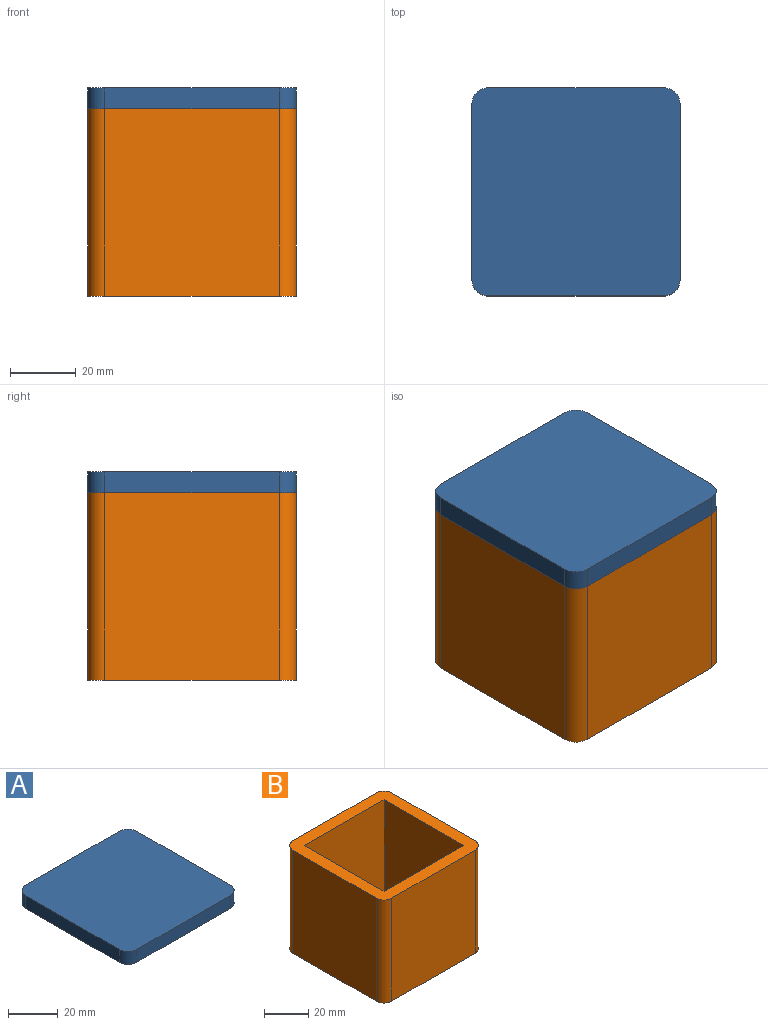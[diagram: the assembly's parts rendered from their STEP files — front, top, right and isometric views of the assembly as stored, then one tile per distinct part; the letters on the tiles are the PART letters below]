
ASSEMBLY  parts=2 mates=1
PART A: 15 faces, bbox 63.5x63.5x12.7 mm
  f0: plane 48.26x6.35mm, normal (1,0,0), area 306.5mm2, adj f1,f3,f4,f10
  f1: plane 48.26x6.35mm, normal (0,1,0), area 306.5mm2, adj f0,f2,f4,f10
  f2: plane 48.26x6.35mm, normal (-1,0,0), area 306.5mm2, adj f1,f3,f4,f10
  f3: plane 48.26x6.35mm, normal (0,-1,0), area 306.5mm2, adj f0,f2,f4,f10
  f4: plane 48.26x48.26mm, normal (0,0,-1), area 2329mm2, adj f0,f1,f2,f3
  f5: plane 53.34x6.35mm, normal (1,0,0), area 338.7mm2, adj f9,f10,f11,f14
  f6: plane 53.34x6.35mm, normal (0,1,0), area 338.7mm2, adj f9,f10,f11,f12
  f7: plane 53.34x6.35mm, normal (-1,0,0), area 338.7mm2, adj f9,f10,f12,f13
  f8: plane 53.34x6.35mm, normal (0,-1,0), area 338.7mm2, adj f9,f10,f13,f14
  f9: plane 63.5x63.5mm, normal (0,0,1), area 4010.1mm2, adj f5,f6,f7,f8,f11,f12,f13,f14
  f10: plane 63.5x63.5mm, normal (0,0,-1), area 1681.1mm2, adj f0,f1,f2,f3,f5,f6,f7,f8
  f11: cylinder r=5.08mm len=6.35mm, axis (0,0,1), area 50.7mm2, adj f5,f6,f9,f10
  f12: cylinder r=5.08mm len=6.35mm, axis (0,0,-1), area 50.7mm2, adj f6,f7,f9,f10
  f13: cylinder r=5.08mm len=6.35mm, axis (0,0,1), area 50.7mm2, adj f7,f8,f9,f10
  f14: cylinder r=5.08mm len=6.35mm, axis (0,0,-1), area 50.7mm2, adj f5,f8,f9,f10
PART B: 15 faces, bbox 63.5x63.5x57.2 mm
  f0: plane 63.5x63.5mm, normal (0,0,1), area 1429.5mm2, adj f1,f2,f3,f4,f5,f6,f7,f8
  f1: plane 57.15x53.34mm, normal (0,-1,0), area 3048.4mm2, adj f0,f10,f11,f13
  f2: plane 57.15x53.34mm, normal (-1,0,0), area 3048.4mm2, adj f0,f10,f11,f12
  f3: plane 57.15x53.34mm, normal (0,1,0), area 3048.4mm2, adj f0,f10,f12,f14
  f4: plane 57.15x53.34mm, normal (1,0,0), area 3048.4mm2, adj f0,f10,f13,f14
  f5: plane 50.8x50.8mm, normal (0,1,0), area 2580.6mm2, adj f0,f6,f8,f9
  f6: plane 50.8x50.8mm, normal (1,0,0), area 2580.6mm2, adj f0,f5,f7,f9
  f7: plane 50.8x50.8mm, normal (0,-1,0), area 2580.6mm2, adj f0,f6,f8,f9
  f8: plane 50.8x50.8mm, normal (-1,0,0), area 2580.6mm2, adj f0,f5,f7,f9
  f9: plane 50.8x50.8mm, normal (0,0,1), area 2580.6mm2, adj f5,f6,f7,f8
  f10: plane 63.5x63.5mm, normal (0,0,-1), area 4010.1mm2, adj f1,f2,f3,f4,f11,f12,f13,f14
  f11: cylinder r=5.08mm len=57.15mm, axis (0,0,1), area 456mm2, adj f0,f1,f2,f10
  f12: cylinder r=5.08mm len=57.15mm, axis (0,0,-1), area 456mm2, adj f0,f2,f3,f10
  f13: cylinder r=5.08mm len=57.15mm, axis (0,0,-1), area 456mm2, adj f0,f1,f4,f10
  f14: cylinder r=5.08mm len=57.15mm, axis (0,0,1), area 456mm2, adj f0,f3,f4,f10
PLACE A t=(-1.27,0,44.45)mm
PLACE B t=(-1.27,0,0)mm
MATE fastened A.f10 <-> B.f0  axis (0,0,-1) through (25.4,-31.75,50.8)mm
